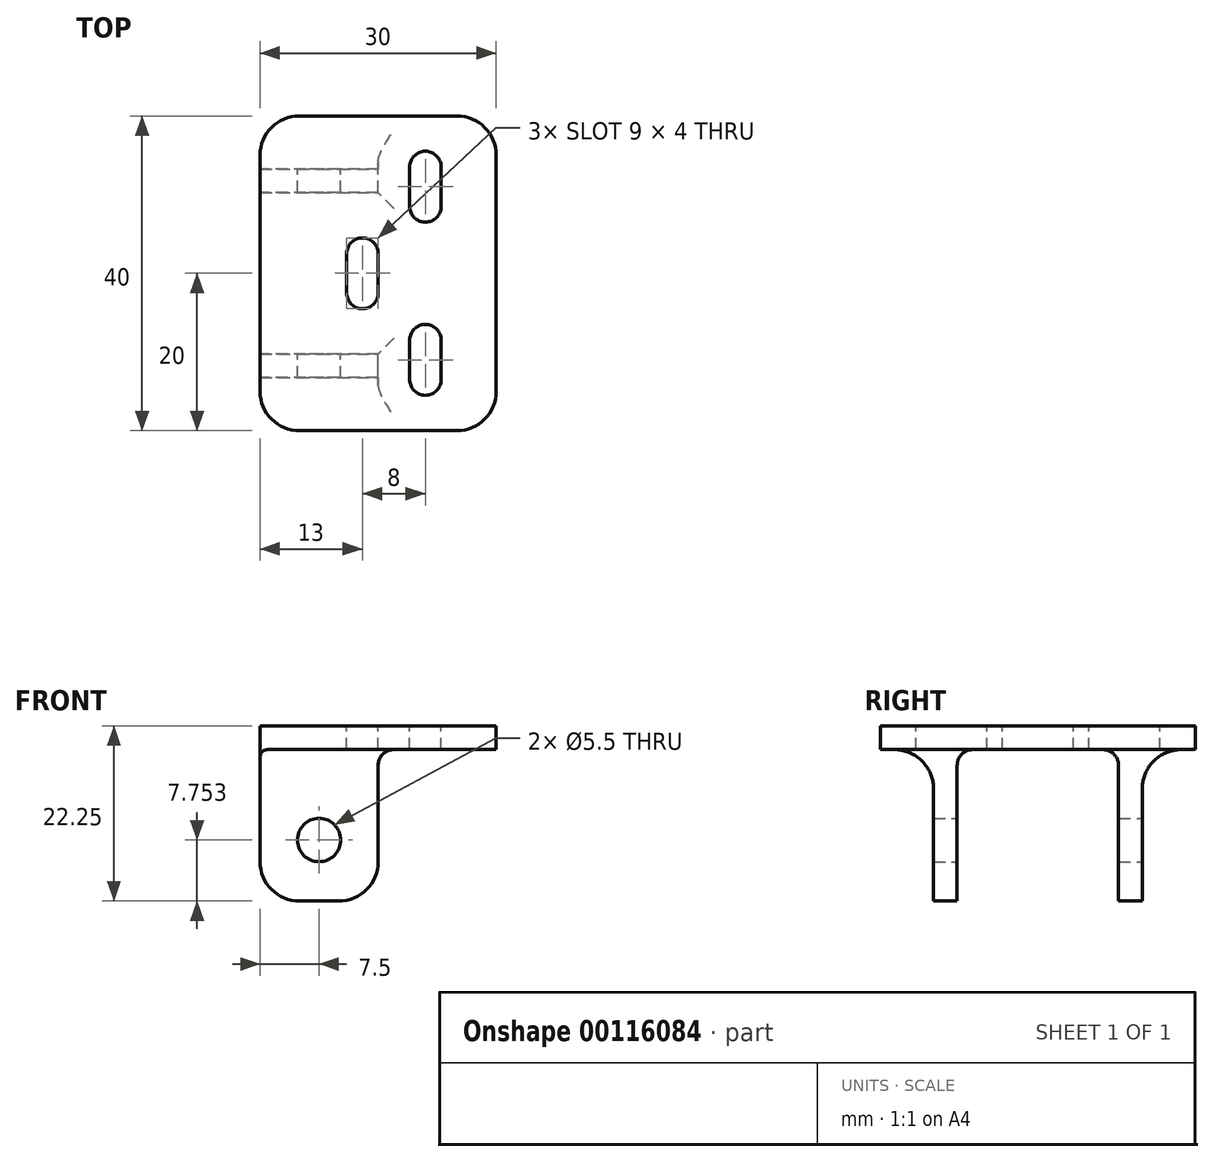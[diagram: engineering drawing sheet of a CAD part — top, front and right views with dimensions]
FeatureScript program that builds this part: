
annotation { "Feature Type Name" : "Feature", "Feature Type Description" : "" }
export const myFeature = defineFeature(function(context is Context, id is Id, definition is map)
    precondition{}
    {
        {
            var Q0;
            Q0=qCreatedBy(makeId("Front.planeOp"),FACE);
            var sketch = newSketch(context, id + "F0", { "sketchPlane" : qUnion([Q0])});
            skPoint(sketch, "E0.middle", {"position": v(0, 0) * mm});
            skLineSegment(sketch, "E1", {"start": v(0, 0) * mm, "end": v(0, 15.23) * mm, "construction": true});
            skCircle(sketch, "E2", {"center": v(0, 0) * mm, "radius": 2.25 * mm});
            skCircle(sketch, "E3", {"center": v(0, -11) * mm, "radius": 2.25 * mm});
            skLineSegment(sketch, "E4", {"start": v(-21, -37.8) * mm, "end": v(31.02, -37.8) * mm, "construction": true});
            skLineSegment(sketch, "E5", {"start": v(31.26, -28.42) * mm, "end": v(-27, -28.43) * mm, "construction": true});
            skLineSegment(sketch, "E6", {"start": v(-65.27, -15.46) * mm, "end": v(32.45, -15.46) * mm, "construction": true});
            skLineSegment(sketch, "E7", {"start": v(25.43, 15.13) * mm, "end": v(72.57, 15.13) * mm, "construction": true});
            skCircle(sketch, "E8", {"center": v(25.43, 15.13) * mm, "radius": 2.55 * mm});
            skCircle(sketch, "E9", {"center": v(-21, 26.8) * mm, "radius": 2.55 * mm});
            skCircle(sketch, "E10", {"center": v(-21, -37.8) * mm, "radius": 3.57 * mm});
            skLineSegment(sketch, "E11", {"start": v(-27, 67.2) * mm, "end": v(-27, -67.3) * mm, "construction": true});
            skLineSegment(sketch, "E12", {"start": v(-27, -67.3) * mm, "end": v(60.77, -67.3) * mm, "construction": true});
            skCircle(sketch, "E13", {"center": v(-20, 56.2) * mm, "radius": 2 * mm, "construction": true});
            skCircle(sketch, "E14", {"center": v(8, 56.2) * mm, "radius": 2 * mm, "construction": true});
            skCircle(sketch, "E15", {"center": v(25.43, 62.27) * mm, "radius": 2.55 * mm});
            skLineSegment(sketch, "E16", {"start": v(77.2, 10.5) * mm, "end": v(20.8, 10.5) * mm, "construction": true});
            skLineSegment(sketch, "E17", {"start": v(20.8, 10.5) * mm, "end": v(20.8, 66.9) * mm, "construction": true});
            skLineSegment(sketch, "E18", {"start": v(20.8, 66.9) * mm, "end": v(77.2, 66.9) * mm, "construction": true});
            skLineSegment(sketch, "E19", {"start": v(25.43, 15.13) * mm, "end": v(25.43, 62.27) * mm, "construction": true});
            skLineSegment(sketch, "E20", {"start": v(25.43, 38.7) * mm, "end": v(49, 38.7) * mm, "construction": true});
            skLineSegment(sketch, "E21", {"start": v(77.2, 10.5) * mm, "end": v(77.2, 66.9) * mm, "construction": true});
            skLineSegment(sketch, "E22", {"start": v(49, 15.13) * mm, "end": v(49, 38.7) * mm, "construction": true});
            skLineSegment(sketch, "E23", {"start": v(-27, 67.2) * mm, "end": v(125, 67.2) * mm, "construction": true});
            skCircle(sketch, "E24", {"center": v(-3.45, -37.8) * mm, "radius": 2 * mm});
            skLineSegment(sketch, "E25.MirrorCS", {"start": v(125, 67.2) * mm, "end": v(125, -67.3) * mm, "construction": true});
            skCircle(sketch, "E26.MirrorC", {"center": v(119, 26.8) * mm, "radius": 2.55 * mm});
            skCircle(sketch, "E27.MirrorC", {"center": v(119, -37.8) * mm, "radius": 3.57 * mm});
            skCircle(sketch, "E28.MirrorC", {"center": v(101.45, -37.8) * mm, "radius": 2 * mm});
            skCircle(sketch, "E29.MirrorC", {"center": v(72.57, 15.13) * mm, "radius": 2.55 * mm});
            skCircle(sketch, "E30.MirrorC", {"center": v(72.57, 62.27) * mm, "radius": 2.55 * mm});
            skSolve(sketch);
        }
        {
            var Q0;
            Q0=qCreatedBy(makeId("Front.planeOp"),FACE);
            var sketch = newSketch(context, id + "F1", { "sketchPlane" : qUnion([Q0])});
            skArc(sketch, "E31", {"start": v(-52.45, 66.8) * mm, "mid": v(-87.45, 31.8) * mm, "end": v(-52.45, -3.2) * mm, "construction": true});
            skLineSegment(sketch, "E32", {"start": v(-52.45, -10.46) * mm, "end": v(-22.45, -10.46) * mm});
            skLineSegment(sketch, "E33", {"start": v(-52.45, 74.04) * mm, "end": v(-22.45, 74.04) * mm});
            skLineSegment(sketch, "E34", {"start": v(-52.45, 4.04) * mm, "end": v(-22.45, 4.04) * mm});
            skLineSegment(sketch, "E35", {"start": v(-52.45, 59.54) * mm, "end": v(-22.45, 59.54) * mm});
            skArc(sketch, "E36", {"start": v(-52.45, 74.04) * mm, "mid": v(-94.7, 31.8) * mm, "end": v(-52.45, -10.46) * mm});
            skArc(sketch, "E37", {"start": v(-52.45, 59.54) * mm, "mid": v(-80.2, 31.8) * mm, "end": v(-52.45, 4.04) * mm});
            skLineSegment(sketch, "E38", {"start": v(-52.45, 74.04) * mm, "end": v(-52.45, 59.54) * mm, "construction": true});
            skLineSegment(sketch, "E39", {"start": v(-52.45, -10.46) * mm, "end": v(-52.45, 4.04) * mm, "construction": true});
            skLineSegment(sketch, "E40", {"start": v(-52.45, -30.46) * mm, "end": v(-22.45, -30.46) * mm});
            skLineSegment(sketch, "E41.bottom", {"start": v(109.28, -47.8) * mm, "end": v(-11.28, -47.8) * mm});
            skLineSegment(sketch, "E41.top", {"start": v(109.28, -27.8) * mm, "end": v(-11.28, -27.8) * mm});
            skLineSegment(sketch, "E41.left", {"start": v(109.28, -47.8) * mm, "end": v(109.28, -27.8) * mm});
            skLineSegment(sketch, "E41.right", {"start": v(-11.28, -47.8) * mm, "end": v(-11.28, -27.8) * mm});
            skPoint(sketch, "E41.middle", {"position": v(49, -37.8) * mm});
            skLineSegment(sketch, "E42", {"start": v(-52.45, -10.46) * mm, "end": v(-52.45, -20.46) * mm});
            skSolve(sketch);
        }
        {
            var Q0;
            Q0=qCreatedBy(makeId("Front.planeOp"),FACE);
            var sketch = newSketch(context, id + "F2", { "sketchPlane" : qUnion([Q0])});
            skLineSegment(sketch, "E43.0", {"start": v(-27, 67.2) * mm, "end": v(-27, -67.3) * mm, "construction": true});
            skLineSegment(sketch, "E44.0", {"start": v(-27, 67.2) * mm, "end": v(125, 67.2) * mm, "construction": true});
            skCircle(sketch, "E45.0", {"center": v(-20, 56.2) * mm, "radius": 2 * mm, "construction": true});
            skLineSegment(sketch, "E46.0", {"start": v(20.8, 10.5) * mm, "end": v(20.8, 66.9) * mm, "construction": true});
            skPoint(sketch, "E47.0", {"position": v(-37.45, -10.46) * mm});
            skLineSegment(sketch, "E48.bottom", {"start": v(-32, -12.46) * mm, "end": v(-47, -12.46) * mm});
            skLineSegment(sketch, "E48.top", {"start": v(-32, -35.46) * mm, "end": v(-47, -35.46) * mm});
            skLineSegment(sketch, "E48.left", {"start": v(-32, -12.46) * mm, "end": v(-32, -35.46) * mm});
            skLineSegment(sketch, "E48.right", {"start": v(-47, -12.46) * mm, "end": v(-47, -35.46) * mm});
            skCircle(sketch, "E49", {"center": v(-39.5, -23.96) * mm, "radius": 2.75 * mm});
            skPoint(sketch, "E49.centerSnap0", {"position": v(-47, -23.96) * mm});
            skLineSegment(sketch, "E50", {"start": v(-47, -23.96) * mm, "end": v(-32, -23.96) * mm, "construction": true});
            skLineSegment(sketch, "E51.0", {"start": v(-65.27, -15.46) * mm, "end": v(32.45, -15.46) * mm, "construction": true});
            skLineSegment(sketch, "E52", {"start": v(-47, -12.46) * mm, "end": v(-47, -9.46) * mm});
            skLineSegment(sketch, "E53", {"start": v(-47, -9.46) * mm, "end": v(-17, -9.46) * mm});
            skLineSegment(sketch, "E54", {"start": v(-17, -9.46) * mm, "end": v(-17, -12.46) * mm});
            skLineSegment(sketch, "E55", {"start": v(-17, -12.46) * mm, "end": v(-32, -12.46) * mm});
            skLineSegment(sketch, "E56", {"start": v(-47, -31.7) * mm, "end": v(-32, -31.7) * mm});
            skSolve(sketch);
        }
        {
            var Q0;
            Q0=makeQuery(id+"F2.imprint","IMPRINT",FACE,{"disambiguationData":[TD([[makeQuery(id+"F2.imprint","IMPRINT",EDGE,{"derivedFrom":sQuery(id+"F2.wireOp",EDGE,"E48.bottom")}),-1.0]])]});
            var Q1;
            Q1=makeQuery(id+"F2.imprint","IMPRINT",FACE,{"disambiguationData":[TD([[makeQuery(id+"F2.imprint","IMPRINT",EDGE,{"derivedFrom":sQuery(id+"F2.wireOp",EDGE,"E48.bottom")}),1.0]])]});
            extrude(context, id + "F3", {"entities" : qUnion([Q0, Q1]), "depth" : 40 * mm, "offsetDistance" : 25 * mm});
        }
        {
            var Q0;
            Q0=makeQuery(id+"F3.opExtrude","SWEPT_FACE",FACE,{"disambiguationData":[OSD([sQuery(id+"F2.wireOp",EDGE,"E53")])]});
            var sketch = newSketch(context, id + "F4", { "sketchPlane" : qUnion([Q0])});
            skLineSegment(sketch, "E57.bottom", {"start": v(-18, -38.5) * mm, "end": v(-47, -38.5) * mm});
            skLineSegment(sketch, "E57.top", {"start": v(-18, -1.5) * mm, "end": v(-47, -1.5) * mm});
            skLineSegment(sketch, "E57.left", {"start": v(-18, -38.5) * mm, "end": v(-18, -1.5) * mm});
            skLineSegment(sketch, "E57.right", {"start": v(-47, -38.5) * mm, "end": v(-47, -1.5) * mm});
            skLineSegment(sketch, "E58", {"start": v(-47, -20) * mm, "end": v(-18, -20) * mm, "construction": true});
            skArc(sketch, "E59", {"start": v(-32, -17.5) * mm, "mid": v(-34, -15.5) * mm, "end": v(-36, -17.5) * mm});
            skLineSegment(sketch, "E60", {"start": v(-36, -17.5) * mm, "end": v(-36, -22.5) * mm});
            skLineSegment(sketch, "E61", {"start": v(-32, -17.5) * mm, "end": v(-32, -22.5) * mm});
            skArc(sketch, "E62.trimOffspring", {"start": v(-36, -22.5) * mm, "mid": v(-34, -24.5) * mm, "end": v(-32, -22.5) * mm});
            skArc(sketch, "E63", {"start": v(-24, -6.5) * mm, "mid": v(-26, -4.5) * mm, "end": v(-28, -6.5) * mm});
            skArc(sketch, "E64", {"start": v(-28, -11.5) * mm, "mid": v(-26, -13.5) * mm, "end": v(-24, -11.5) * mm});
            skLineSegment(sketch, "E65", {"start": v(-28, -11.5) * mm, "end": v(-28, -6.5) * mm});
            skLineSegment(sketch, "E66", {"start": v(-28, -6.5) * mm, "end": v(-28, -6.5) * mm});
            skLineSegment(sketch, "E67", {"start": v(-24, -6.5) * mm, "end": v(-24, -11.5) * mm});
            skLineSegment(sketch, "E68", {"start": v(-26, -15.5) * mm, "end": v(-34, -15.5) * mm, "construction": true});
            skPoint(sketch, "E68.endSnap0", {"position": v(-26, -13.5) * mm});
            skLineSegment(sketch, "E69.MirrorCS", {"start": v(-24, -33.5) * mm, "end": v(-24, -28.5) * mm});
            skLineSegment(sketch, "E70.MirrorCS", {"start": v(-28, -28.5) * mm, "end": v(-28, -33.5) * mm});
            skArc(sketch, "E71.MirrorCS", {"start": v(-24, -33.5) * mm, "mid": v(-26, -35.5) * mm, "end": v(-28, -33.5) * mm});
            skArc(sketch, "E72.MirrorCS", {"start": v(-28, -28.5) * mm, "mid": v(-26, -26.5) * mm, "end": v(-24, -28.5) * mm});
            skSolve(sketch);
        }
        {
            var Q0;
            Q0=makeQuery(id+"F4.imprint","IMPRINT",FACE,{"disambiguationData":[TD([[makeQuery(id+"F4.imprint","IMPRINT",EDGE,{"derivedFrom":sQuery(id+"F4.wireOp",EDGE,"E63")}),1.0]])]});
            var Q1;
            Q1=makeQuery(id+"F4.imprint","IMPRINT",FACE,{"disambiguationData":[TD([[makeQuery(id+"F4.imprint","IMPRINT",EDGE,{"derivedFrom":sQuery(id+"F4.wireOp",EDGE,"E59")}),1.0]])]});
            var Q2;
            Q2=makeQuery(id+"F4.imprint","IMPRINT",FACE,{"disambiguationData":[TD([[makeQuery(id+"F4.imprint","IMPRINT",EDGE,{"derivedFrom":sQuery(id+"F4.wireOp",EDGE,"E69.MirrorCS")}),1.0]])]});
            extrude(context, id + "F5", {"entities" : qUnion([Q0, Q1, Q2]), "operationType" : NewBodyOperationType.REMOVE, "endBound" : BoundingType.THROUGH_ALL, "oppositeDirection" : true, "depth" : 25 * mm, "offsetDistance" : 25 * mm});
        }
        {
            var Q0;
            Q0=makeQuery(id+"F3.opExtrude","SWEPT_FACE",FACE,{"disambiguationData":[OSD([sQuery(id+"F2.wireOp",EDGE,"E48.right"),sQuery(id+"F2.wireOp",EDGE,"E52")])]});
            var sketch = newSketch(context, id + "F6", { "sketchPlane" : qUnion([Q0])});
            skLineSegment(sketch, "E73", {"start": v(20, -31.7) * mm, "end": v(20, -9.46) * mm, "construction": true});
            skLineSegment(sketch, "E74.bottom", {"start": v(30.25, -31.7) * mm, "end": v(9.75, -31.7) * mm});
            skLineSegment(sketch, "E74.top", {"start": v(30.25, -12.46) * mm, "end": v(9.75, -12.46) * mm});
            skLineSegment(sketch, "E74.left", {"start": v(30.25, -31.7) * mm, "end": v(30.25, -12.46) * mm});
            skLineSegment(sketch, "E74.right", {"start": v(9.75, -31.7) * mm, "end": v(9.75, -12.46) * mm});
            skLineSegment(sketch, "E75.0", {"start": v(17.5, -12.46) * mm, "end": v(0, -12.46) * mm, "construction": true});
            skLineSegment(sketch, "E76.bottom", {"start": v(40, -31.7) * mm, "end": v(33.25, -31.7) * mm});
            skLineSegment(sketch, "E76.top", {"start": v(40, -12.46) * mm, "end": v(33.25, -12.46) * mm});
            skLineSegment(sketch, "E76.left", {"start": v(40, -31.7) * mm, "end": v(40, -12.46) * mm});
            skLineSegment(sketch, "E76.right", {"start": v(33.25, -31.7) * mm, "end": v(33.25, -12.46) * mm});
            skLineSegment(sketch, "E77.MirrorCS", {"start": v(0, -31.7) * mm, "end": v(6.75, -31.7) * mm});
            skLineSegment(sketch, "E78.MirrorCS", {"start": v(0, -31.7) * mm, "end": v(0, -12.46) * mm});
            skLineSegment(sketch, "E79.MirrorCS", {"start": v(0, -12.46) * mm, "end": v(6.75, -12.46) * mm});
            skLineSegment(sketch, "E80.MirrorCS", {"start": v(6.75, -31.7) * mm, "end": v(6.75, -12.46) * mm});
            skSolve(sketch);
        }
        {
            var Q0;
            Q0=makeQuery(id+"F6.imprint","IMPRINT",FACE,{"disambiguationData":[TD([[makeQuery(id+"F6.imprint","IMPRINT",EDGE,{"derivedFrom":sQuery(id+"F6.wireOp",EDGE,"E77.MirrorCS")}),-1.0]])]});
            var Q1;
            Q1=makeQuery(id+"F6.imprint","IMPRINT",FACE,{"disambiguationData":[TD([[makeQuery(id+"F6.imprint","IMPRINT",EDGE,{"derivedFrom":sQuery(id+"F6.wireOp",EDGE,"E74.bottom")}),-1.0]])]});
            var Q2;
            Q2=makeQuery(id+"F6.imprint","IMPRINT",FACE,{"disambiguationData":[TD([[makeQuery(id+"F6.imprint","IMPRINT",EDGE,{"derivedFrom":sQuery(id+"F6.wireOp",EDGE,"E76.bottom")}),-1.0]])]});
            extrude(context, id + "F7", {"entities" : qUnion([Q0, Q1, Q2]), "operationType" : NewBodyOperationType.REMOVE, "endBound" : BoundingType.THROUGH_ALL, "oppositeDirection" : true, "depth" : 2 * mm, "offsetDistance" : 25 * mm});
        }
        {
            var Q0;
            Q0=makeQuery(id+"F3.opExtrude","CAP_EDGE",EDGE,{"disambiguationData":[OSD([sQuery(id+"F2.wireOp",EDGE,"E54")])],"isStart":true});
            var Q1;
            Q1=makeQuery(id+"F3.opExtrude","CAP_EDGE",EDGE,{"disambiguationData":[OSD([sQuery(id+"F2.wireOp",EDGE,"E54")])],"isStart":false});
            var Q2;
            Q2=makeQuery(id+"F3.opExtrude","CAP_EDGE",EDGE,{"disambiguationData":[OSD([sQuery(id+"F2.wireOp",EDGE,"E48.right"),sQuery(id+"F2.wireOp",EDGE,"E52")])],"isStart":true});
            var Q3;
            Q3=makeQuery(id+"F3.opExtrude","CAP_EDGE",EDGE,{"disambiguationData":[OSD([sQuery(id+"F2.wireOp",EDGE,"E48.right"),sQuery(id+"F2.wireOp",EDGE,"E52")])],"isStart":false});
            var Q4;
            {var subQ0=sQuery(id+"F2.wireOp",EDGE,"E48.top");var subQ1=sQuery(id+"F2.wireOp",EDGE,"E48.left");Q4=makeQuery(id+"F5.boolean.opBoolean","SPLIT",EDGE,{"disambiguationData":[TD([makeQuery(id+"F5.opExtrude","SWEPT_FACE",FACE,{"disambiguationData":[OSD([sQuery(id+"F4.wireOp",EDGE,"E62.trimOffspring")])]})])],"derivedFrom":makeQuery(id+"F3.opExtrude","SWEPT_EDGE",EDGE,{"disambiguationData":[OSD([subQ0,subQ1])]})});}
            var Q5;
            {var subQ0=sQuery(id+"F2.wireOp",EDGE,"E48.top");var subQ1=sQuery(id+"F2.wireOp",EDGE,"E48.right");Q5=makeQuery(id+"F7.boolean.opBoolean","SPLIT",EDGE,{"disambiguationData":[TD([makeQuery(id+"F7.opExtrude","SWEPT_FACE",FACE,{"disambiguationData":[OSD([sQuery(id+"F6.wireOp",EDGE,"E74.left")])]})])],"derivedFrom":makeQuery(id+"F3.opExtrude","SWEPT_EDGE",EDGE,{"disambiguationData":[OSD([subQ0,subQ1])]})});}
            var Q6;
            {var subQ0=sQuery(id+"F2.wireOp",EDGE,"E48.top");var subQ1=sQuery(id+"F2.wireOp",EDGE,"E48.right");Q6=makeQuery(id+"F7.boolean.opBoolean","SPLIT",EDGE,{"disambiguationData":[TD([makeQuery(id+"F7.opExtrude","SWEPT_FACE",FACE,{"disambiguationData":[OSD([sQuery(id+"F6.wireOp",EDGE,"E74.right")])]})])],"derivedFrom":makeQuery(id+"F3.opExtrude","SWEPT_EDGE",EDGE,{"disambiguationData":[OSD([subQ0,subQ1])]})});}
            var Q7;
            {var subQ0=sQuery(id+"F2.wireOp",EDGE,"E48.top");var subQ1=sQuery(id+"F2.wireOp",EDGE,"E48.left");Q7=makeQuery(id+"F5.boolean.opBoolean","SPLIT",EDGE,{"disambiguationData":[TD([makeQuery(id+"F5.opExtrude","SWEPT_FACE",FACE,{"disambiguationData":[OSD([sQuery(id+"F4.wireOp",EDGE,"E59")])]})])],"derivedFrom":makeQuery(id+"F3.opExtrude","SWEPT_EDGE",EDGE,{"disambiguationData":[OSD([subQ0,subQ1])]})});}
            fillet(context, id + "F8", {"entities" : qUnion([Q0, Q1, Q2, Q3, Q4, Q5, Q6, Q7]), "radius" : 5 * mm, "tangentPropagation" : true, "allowEdgeOverflow" : false});
        }
        {
            var Q0;
            Q0=makeQuery(id+"F7.boolean.opBoolean","COPY",EDGE,{"derivedFrom":makeQuery(id+"F7.opExtrude","SWEPT_EDGE",EDGE,{"disambiguationData":[OSD([sQuery(id+"F6.wireOp",EDGE,"E76.top"),sQuery(id+"F6.wireOp",EDGE,"E76.right")])]})});
            var Q1;
            Q1=makeQuery(id+"F7.boolean.opBoolean","COPY",EDGE,{"derivedFrom":makeQuery(id+"F7.opExtrude","SWEPT_EDGE",EDGE,{"disambiguationData":[OSD([sQuery(id+"F6.wireOp",EDGE,"E79.MirrorCS"),sQuery(id+"F6.wireOp",EDGE,"E80.MirrorCS")])]})});
            fillet(context, id + "F9", {"entities" : qUnion([Q0, Q1]), "radius" : 5 * mm, "tangentPropagation" : true, "allowEdgeOverflow" : false});
        }
        {
            var Q0;
            {var subQ0=sQuery(id+"F2.wireOp",EDGE,"E55");var subQ1=makeQuery(id+"F3.opExtrude","SWEPT_FACE",FACE,{"disambiguationData":[OSD([subQ0])]});var subQ2=sQuery(id+"F2.wireOp",EDGE,"E48.left");var subQ3=makeQuery(id+"F3.opExtrude","SWEPT_FACE",FACE,{"disambiguationData":[OSD([subQ2])]});Q0=makeQuery(id+"F5.boolean.opBoolean","SPLIT",EDGE,{"disambiguationData":[topologyDisambiguationEdgeConnected([subQ3,subQ1]),TD([makeQuery(id+"F5.opExtrude","SWEPT_FACE",FACE,{"disambiguationData":[OSD([sQuery(id+"F4.wireOp",EDGE,"E62.trimOffspring")])]})])],"derivedFrom":makeQuery(id+"F3.opExtrude","SWEPT_EDGE",EDGE,{"disambiguationData":[OSD([sQuery(id+"F2.wireOp",EDGE,"E48.bottom"),subQ2,subQ0])]})});}
            var Q1;
            {var subQ0=sQuery(id+"F2.wireOp",EDGE,"E55");var subQ1=sQuery(id+"F2.wireOp",EDGE,"E48.left");var subQ2=makeQuery(id+"F3.opExtrude","SWEPT_FACE",FACE,{"disambiguationData":[OSD([subQ0])]});var subQ3=makeQuery(id+"F3.opExtrude","SWEPT_FACE",FACE,{"disambiguationData":[OSD([subQ1])]});Q1=makeQuery(id+"F5.boolean.opBoolean","SPLIT",EDGE,{"disambiguationData":[topologyDisambiguationEdgeConnected([subQ3,subQ2]),TD([makeQuery(id+"F5.opExtrude","SWEPT_FACE",FACE,{"disambiguationData":[OSD([sQuery(id+"F4.wireOp",EDGE,"E59")])]})])],"derivedFrom":makeQuery(id+"F3.opExtrude","SWEPT_EDGE",EDGE,{"disambiguationData":[OSD([sQuery(id+"F2.wireOp",EDGE,"E48.bottom"),subQ1,subQ0])]})});}
            var Q2;
            Q2=makeQuery(id+"F7.boolean.opBoolean","COPY",EDGE,{"derivedFrom":makeQuery(id+"F7.opExtrude","SWEPT_EDGE",EDGE,{"disambiguationData":[OSD([sQuery(id+"F6.wireOp",EDGE,"E74.top"),sQuery(id+"F6.wireOp",EDGE,"E74.left")])]})});
            var Q3;
            Q3=makeQuery(id+"F7.boolean.opBoolean","COPY",EDGE,{"derivedFrom":makeQuery(id+"F7.opExtrude","SWEPT_EDGE",EDGE,{"disambiguationData":[OSD([sQuery(id+"F6.wireOp",EDGE,"E74.top"),sQuery(id+"F6.wireOp",EDGE,"E74.right")])]})});
            fillet(context, id + "F10", {"entities" : qUnion([Q0, Q1, Q2, Q3]), "radius" : 2 * mm, "tangentPropagation" : true, "allowEdgeOverflow" : false});
        }
    });
